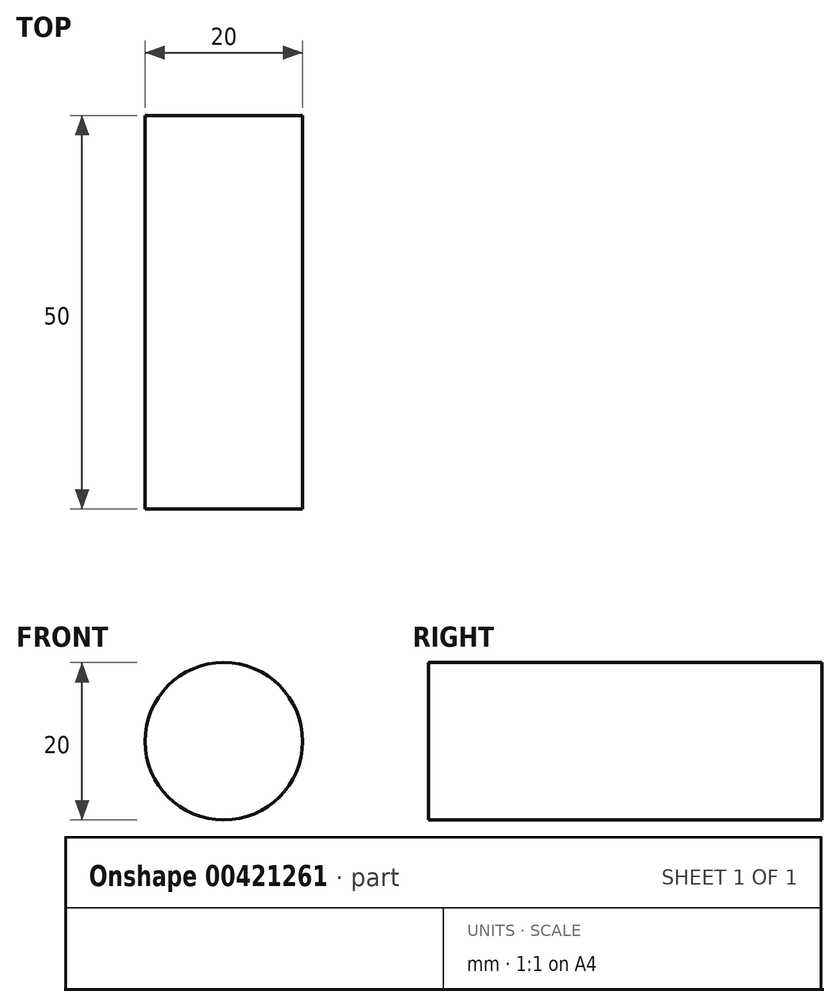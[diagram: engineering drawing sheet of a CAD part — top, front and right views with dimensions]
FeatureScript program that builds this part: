
annotation { "Feature Type Name" : "Feature", "Feature Type Description" : "" }
export const myFeature = defineFeature(function(context is Context, id is Id, definition is map)
    precondition{}
    {
        {
            var Q0;
            Q0=qCreatedBy(makeId("Front.planeOp"),FACE);
            var sketch = newSketch(context, id + "F0", { "sketchPlane" : qUnion([Q0])});
            skCircle(sketch, "E0", {"center": v(0, 0) * mm, "radius": 10 * mm});
            skSolve(sketch);
        }
        {
            var Q0;
            Q0=makeQuery(id+"F0.imprint","IMPRINT",FACE,{"disambiguationData":[TD([[makeQuery(id+"F0.imprint","IMPRINT",EDGE,{"derivedFrom":sQuery(id+"F0.wireOp",EDGE,"E0")}),1.0]])]});
            extrude(context, id + "F1", {"entities" : qUnion([Q0]), "depth" : 50 * mm, "offsetDistance" : 25 * mm});
        }
    });
